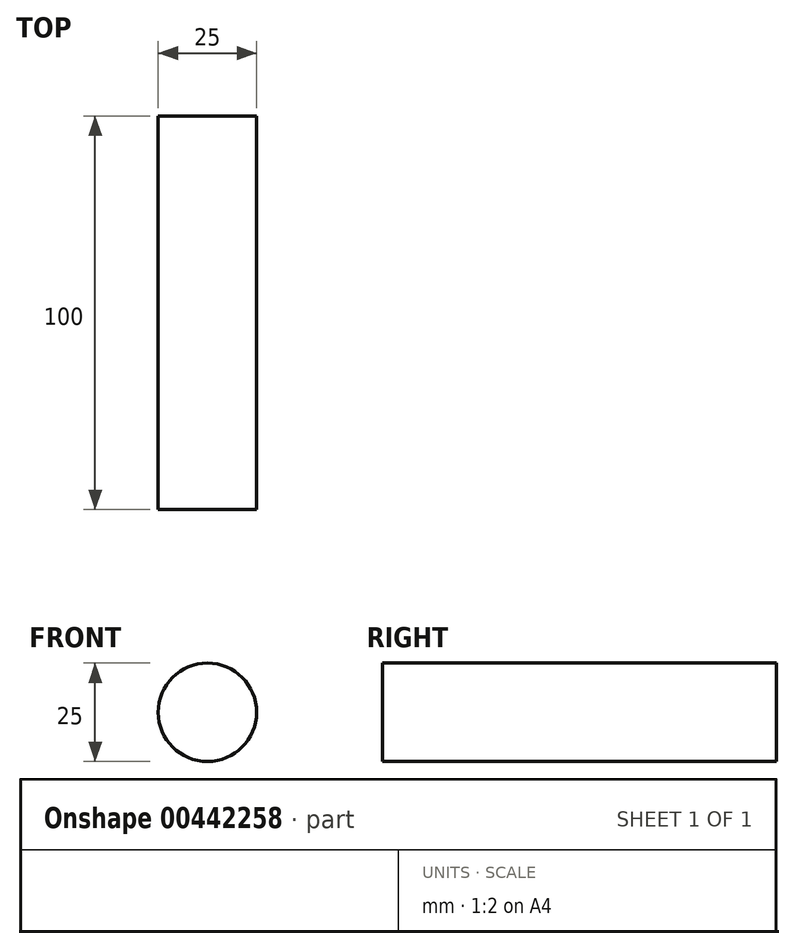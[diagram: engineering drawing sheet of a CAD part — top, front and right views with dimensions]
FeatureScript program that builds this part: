
annotation { "Feature Type Name" : "Feature", "Feature Type Description" : "" }
export const myFeature = defineFeature(function(context is Context, id is Id, definition is map)
    precondition{}
    {
        {
            var Q0;
            Q0=qCreatedBy(makeId("Front.planeOp"),FACE);
            var sketch = newSketch(context, id + "F0", { "sketchPlane" : qUnion([Q0])});
            skCircle(sketch, "E0", {"center": v(0, 0) * mm, "radius": 12.5 * mm});
            skSolve(sketch);
        }
        {
            var Q0;
            Q0=makeQuery(id+"F0.imprint","IMPRINT",FACE,{"disambiguationData":[TD([[makeQuery(id+"F0.imprint","IMPRINT",EDGE,{"derivedFrom":sQuery(id+"F0.wireOp",EDGE,"E0")}),1.0]])]});
            extrude(context, id + "F1", {"entities" : qUnion([Q0]), "endBound" : BoundingType.SYMMETRIC, "depth" : 100 * mm});
        }
    });
